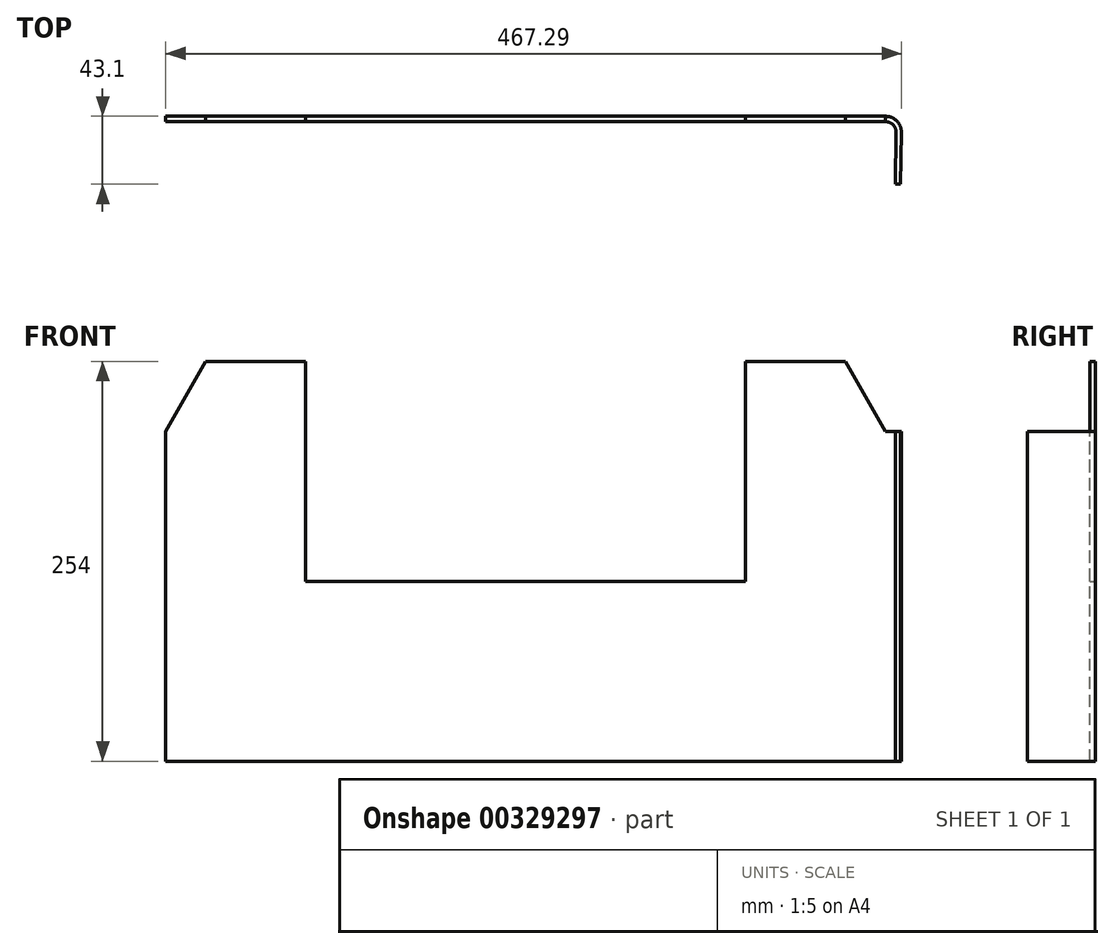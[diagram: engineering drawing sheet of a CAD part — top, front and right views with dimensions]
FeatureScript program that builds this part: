
annotation { "Feature Type Name" : "Feature", "Feature Type Description" : "" }
export const myFeature = defineFeature(function(context is Context, id is Id, definition is map)
    precondition{}
    {
        {
            var Q0;
            Q0=qCreatedBy(makeId("Front.planeOp"),FACE);
            var sketch = newSketch(context, id + "F0", { "sketchPlane" : qUnion([Q0])});
            skLineSegment(sketch, "E0", {"start": v(-228.6, -152.4) * mm, "end": v(-228.6, 57.15) * mm});
            skLineSegment(sketch, "E1", {"start": v(-228.6, 57.15) * mm, "end": v(-203.2, 101.6) * mm});
            skLineSegment(sketch, "E2", {"start": v(-203.2, 101.6) * mm, "end": v(-139.7, 101.6) * mm});
            skLineSegment(sketch, "E3", {"start": v(-139.7, 101.6) * mm, "end": v(-139.7, -38.1) * mm});
            skLineSegment(sketch, "E4", {"start": v(-139.7, -38.1) * mm, "end": v(139.7, -38.1) * mm});
            skLineSegment(sketch, "E5", {"start": v(139.7, -38.1) * mm, "end": v(139.7, 101.6) * mm});
            skLineSegment(sketch, "E6", {"start": v(139.7, 101.6) * mm, "end": v(203.2, 101.6) * mm});
            skLineSegment(sketch, "E7", {"start": v(203.2, 101.6) * mm, "end": v(228.6, 57.15) * mm});
            skLineSegment(sketch, "E8", {"start": v(228.6, 57.15) * mm, "end": v(228.6, -152.4) * mm});
            skLineSegment(sketch, "E9", {"start": v(228.6, -152.4) * mm, "end": v(-228.6, -152.4) * mm});
            skSolve(sketch);
        }
        {
            var Q0;
            Q0 = qSketchRegion(id + "F0", true);
            extrude(context, id + "F1", {"entities" : qUnion([Q0]), "depth" : 3.42 * mm});
        }
        {
            var Q0;
            Q0=makeQuery(id+"F1.opExtrude","SWEPT_FACE",FACE,{"disambiguationData":[OSD([sQuery(id+"F0.wireOp",EDGE,"E9")])]});
            var sketch = newSketch(context, id + "F2", { "sketchPlane" : qUnion([Q0])});
            skArc(sketch, "E10", {"start": v(228.6, 3.42) * mm, "mid": v(233.4, 5.43) * mm, "end": v(235.33, 10.27) * mm});
            skLineSegment(sketch, "E11", {"start": v(235.33, 10.27) * mm, "end": v(234.73, 43.04) * mm});
            skLineSegment(sketch, "E12", {"start": v(234.73, 43.04) * mm, "end": v(238.08, 43.1) * mm});
            skLineSegment(sketch, "E13", {"start": v(238.08, 43.1) * mm, "end": v(238.69, 10.27) * mm});
            skArc(sketch, "E14", {"start": v(228.6, 0) * mm, "mid": v(235.8, 3.02) * mm, "end": v(238.69, 10.27) * mm});
            skLineSegment(sketch, "E15", {"start": v(228.6, 0) * mm, "end": v(228.6, 3.42) * mm});
            skSolve(sketch);
        }
        {
            var Q0;
            Q0 = qSketchRegion(id + "F2", true);
            var Q1;
            Q1=makeQuery(id+"F1.opExtrude","CAP_VERTEX",VERTEX,{"disambiguationData":[OSD([sQuery(id+"F0.wireOp",EDGE,"E7"),sQuery(id+"F0.wireOp",EDGE,"E8")])],"isStart":false});
            extrude(context, id + "F3", {"entities" : qUnion([Q0]), "operationType" : NewBodyOperationType.ADD, "endBound" : BoundingType.UP_TO_VERTEX, "oppositeDirection" : true, "endBoundEntityVertex" : qUnion([Q1]), "depth" : 25.4 * mm});
        }
    });
